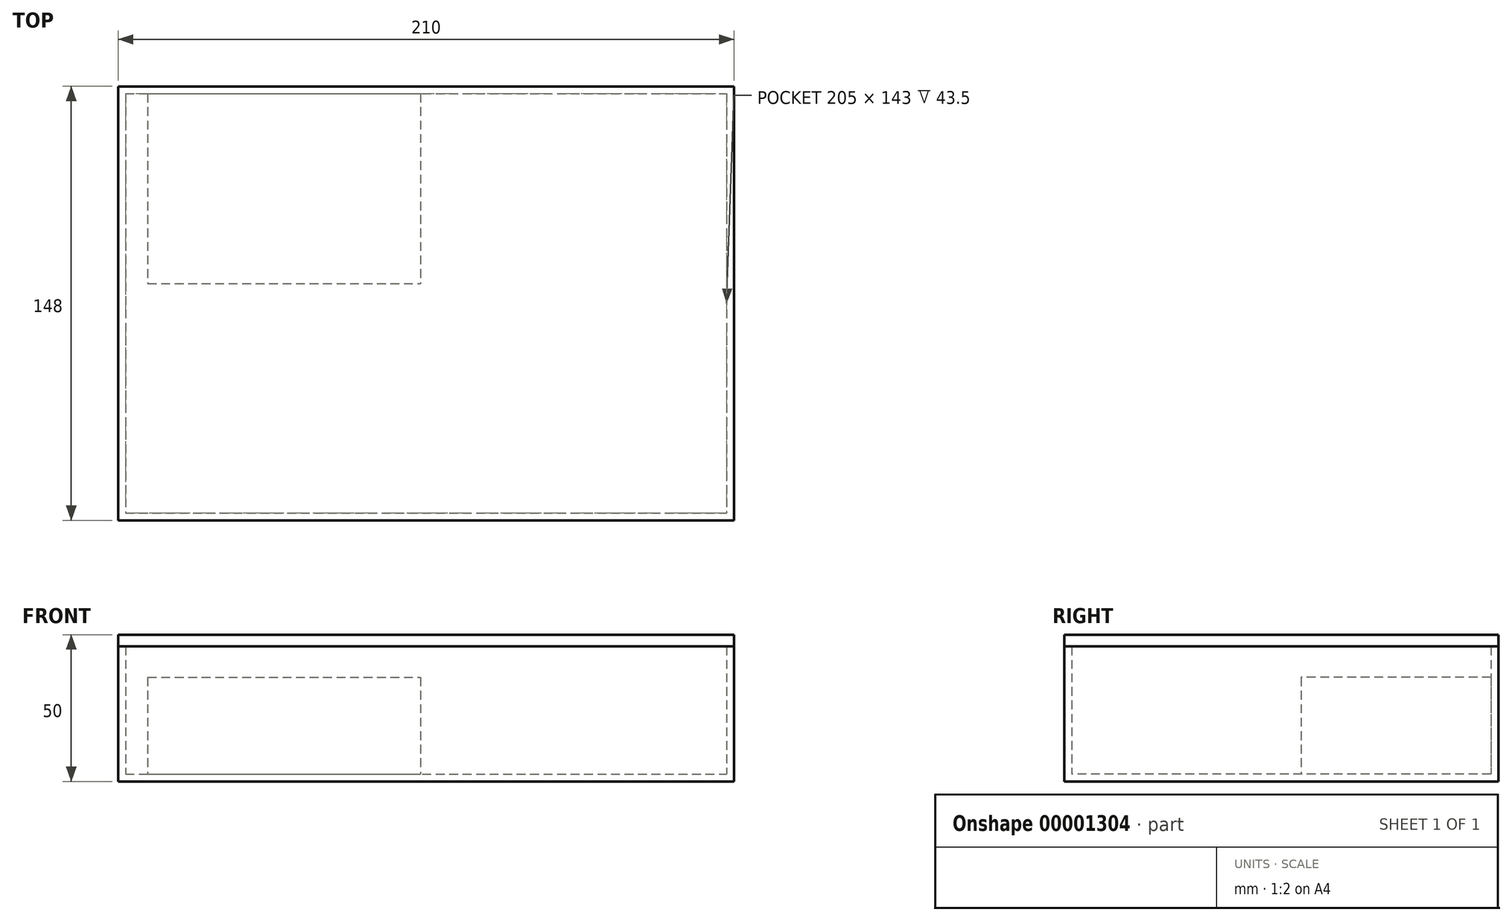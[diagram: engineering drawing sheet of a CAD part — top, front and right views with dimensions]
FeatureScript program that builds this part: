
annotation { "Feature Type Name" : "Feature", "Feature Type Description" : "" }
export const myFeature = defineFeature(function(context is Context, id is Id, definition is map)
    precondition{}
    {
        {
            var Q0;
            Q0=qCreatedBy(makeId("Top.planeOp"),FACE);
            var sketch = newSketch(context, id + "F0", { "sketchPlane" : qUnion([Q0])});
            skLineSegment(sketch, "E0.bottom", {"start": v(-225.37, 29.5) * mm, "end": v(-15.37, 29.5) * mm});
            skLineSegment(sketch, "E0.top", {"start": v(-225.37, -118.5) * mm, "end": v(-15.37, -118.5) * mm});
            skLineSegment(sketch, "E0.left", {"start": v(-225.37, 29.5) * mm, "end": v(-225.37, -118.5) * mm});
            skLineSegment(sketch, "E0.right", {"start": v(-15.37, 29.5) * mm, "end": v(-15.37, -118.5) * mm});
            skSolve(sketch);
        }
        {
            var Q0;
            Q0=makeQuery(id+"F0.imprint","IMPRINT",FACE,{"disambiguationData":[TD([[makeQuery(id+"F0.imprint","IMPRINT",EDGE,{"derivedFrom":sQuery(id+"F0.wireOp",EDGE,"E0.bottom")}),-1.0]])]});
            extrude(context, id + "F1", {"entities" : qUnion([Q0]), "depth" : 46 * mm});
        }
        {
            var Q0;
            Q0=makeQuery(id+"F1.opExtrude","CAP_FACE",FACE,{"disambiguationData":[OSD([sQuery(id+"F0.wireOp",EDGE,"E0.bottom"),sQuery(id+"F0.wireOp",EDGE,"E0.top"),sQuery(id+"F0.wireOp",EDGE,"E0.left"),sQuery(id+"F0.wireOp",EDGE,"E0.right")])],"isStart":false});
            shell(context, id + "F2", {"entities" : qUnion([Q0]), "thickness" : 2.5 * mm});
        }
        {
            var Q0;
            Q0=makeQuery(id+"F1.opExtrude","CAP_FACE",FACE,{"disambiguationData":[OSD([sQuery(id+"F0.wireOp",EDGE,"E0.bottom"),sQuery(id+"F0.wireOp",EDGE,"E0.top"),sQuery(id+"F0.wireOp",EDGE,"E0.left"),sQuery(id+"F0.wireOp",EDGE,"E0.right")])],"isStart":false});
            var sketch = newSketch(context, id + "F3", { "sketchPlane" : qUnion([Q0])});
            skLineSegment(sketch, "E1.bottom", {"start": v(-225.37, -118.5) * mm, "end": v(-15.37, -118.5) * mm});
            skLineSegment(sketch, "E1.top", {"start": v(-225.37, 29.5) * mm, "end": v(-15.37, 29.5) * mm});
            skLineSegment(sketch, "E1.left", {"start": v(-225.37, -118.5) * mm, "end": v(-225.37, 29.5) * mm});
            skLineSegment(sketch, "E1.right", {"start": v(-15.37, -118.5) * mm, "end": v(-15.37, 29.5) * mm});
            skSolve(sketch);
        }
        {
            var Q0;
            Q0 = qSketchRegion(id + "F3", true);
            extrude(context, id + "F4", {"entities" : qUnion([Q0]), "depth" : 4 * mm});
        }
        {
            var Q0;
            Q0=makeQuery(id+"F2.opShell","OFFSET_FACE",FACE,{"disambiguationData":[OSD([sQuery(id+"F0.wireOp",EDGE,"E0.bottom"),sQuery(id+"F0.wireOp",EDGE,"E0.top"),sQuery(id+"F0.wireOp",EDGE,"E0.left"),sQuery(id+"F0.wireOp",EDGE,"E0.right")])]});
            var sketch = newSketch(context, id + "F5", { "sketchPlane" : qUnion([Q0])});
            skLineSegment(sketch, "E2.bottom", {"start": v(-215.3, 28.3) * mm, "end": v(-122.3, 28.3) * mm});
            skLineSegment(sketch, "E2.top", {"start": v(-215.3, -37.7) * mm, "end": v(-122.3, -37.7) * mm});
            skLineSegment(sketch, "E2.left", {"start": v(-215.3, 28.3) * mm, "end": v(-215.3, -37.7) * mm});
            skLineSegment(sketch, "E2.right", {"start": v(-122.3, 28.3) * mm, "end": v(-122.3, -37.7) * mm});
            skSolve(sketch);
        }
        {
            var Q0;
            {var subQ6=sQuery(id+"F5.wireOp",EDGE,"E2.top");Q0=makeQuery(id+"F5.imprint","IMPRINT",FACE,{"disambiguationData":[TD([[makeQuery(id+"F5.imprint","IMPRINT",EDGE,{"derivedFrom":subQ6}),1.0]])]});}
            extrude(context, id + "F6", {"entities" : qUnion([Q0]), "depth" : 33 * mm});
        }
    });
